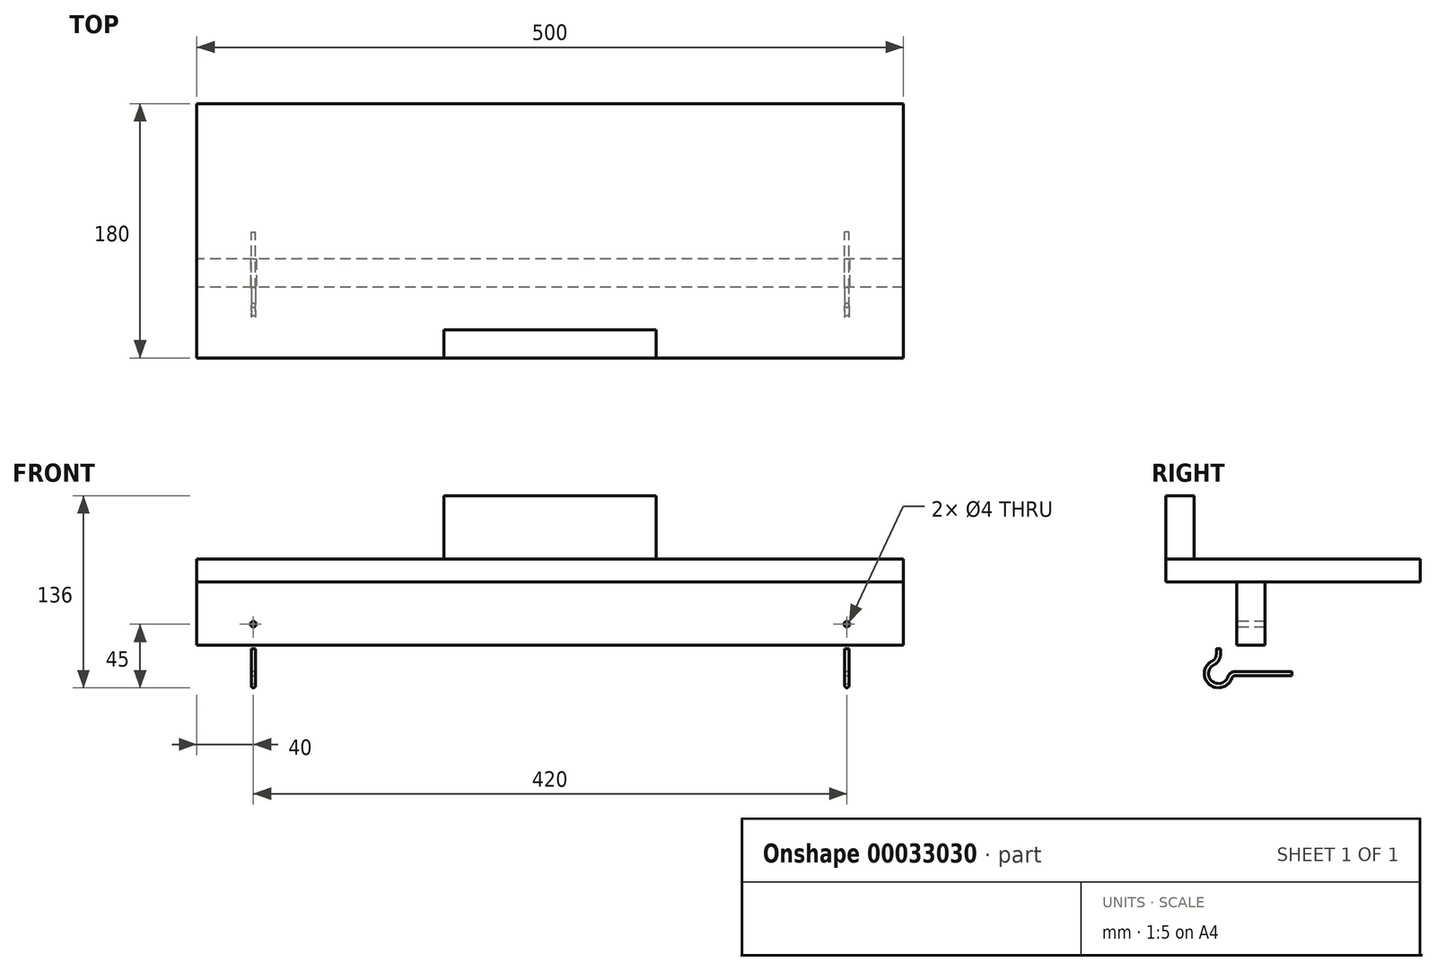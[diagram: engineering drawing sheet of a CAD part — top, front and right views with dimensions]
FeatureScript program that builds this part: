
annotation { "Feature Type Name" : "Feature", "Feature Type Description" : "" }
export const myFeature = defineFeature(function(context is Context, id is Id, definition is map)
    precondition{}
    {
        {
            var Q0;
            Q0=qCreatedBy(makeId("Right.planeOp"),FACE);
            var sketch = newSketch(context, id + "F0", { "sketchPlane" : qUnion([Q0])});
            skLineSegment(sketch, "E0.bottom", {"start": v(0, 0) * mm, "end": v(-180, 0) * mm});
            skLineSegment(sketch, "E0.top", {"start": v(0, -16) * mm, "end": v(-180, -16) * mm});
            skLineSegment(sketch, "E0.left", {"start": v(0, 0) * mm, "end": v(0, -16) * mm});
            skLineSegment(sketch, "E0.right", {"start": v(-180, 0) * mm, "end": v(-180, -16) * mm});
            skSolve(sketch);
        }
        {
            var Q0;
            Q0 = qSketchRegion(id + "F0", true);
            extrude(context, id + "F1", {"entities" : qUnion([Q0]), "endBound" : BoundingType.SYMMETRIC, "depth" : 500 * mm});
        }
        {
            var Q0;
            Q0=qCreatedBy(makeId("Right.planeOp"),FACE);
            var sketch = newSketch(context, id + "F2", { "sketchPlane" : qUnion([Q0])});
            skLineSegment(sketch, "E1.bottom", {"start": v(-130, -16) * mm, "end": v(-110, -16) * mm});
            skLineSegment(sketch, "E1.top", {"start": v(-130, -61) * mm, "end": v(-110, -61) * mm});
            skLineSegment(sketch, "E1.left", {"start": v(-130, -16) * mm, "end": v(-130, -61) * mm});
            skLineSegment(sketch, "E1.right", {"start": v(-110, -16) * mm, "end": v(-110, -61) * mm});
            skSolve(sketch);
        }
        {
            var Q0;
            Q0 = qSketchRegion(id + "F2", true);
            var Q1;
            Q1=makeQuery(id+"F1.opExtrude","CAP_FACE",FACE,{"disambiguationData":[OSD([sQuery(id+"F0.wireOp",EDGE,"E0.bottom"),sQuery(id+"F0.wireOp",EDGE,"E0.top"),sQuery(id+"F0.wireOp",EDGE,"E0.left"),sQuery(id+"F0.wireOp",EDGE,"E0.right")])],"isStart":false});
            var Q2;
            Q2=makeQuery(id+"F1.opExtrude","CAP_FACE",FACE,{"disambiguationData":[OSD([sQuery(id+"F0.wireOp",EDGE,"E0.bottom"),sQuery(id+"F0.wireOp",EDGE,"E0.top"),sQuery(id+"F0.wireOp",EDGE,"E0.left"),sQuery(id+"F0.wireOp",EDGE,"E0.right")])],"isStart":true});
            extrude(context, id + "F3", {"entities" : qUnion([Q0]), "endBound" : BoundingType.UP_TO_SURFACE, "endBoundEntityFace" : qUnion([Q1]), "depth" : 25 * mm, "hasSecondDirection" : true, "secondDirectionBound" : SecondDirectionBoundingType.UP_TO_SURFACE, "secondDirectionOppositeDirection" : true, "secondDirectionBoundEntityFace" : qUnion([Q2]), "secondDirectionDepth" : 25 * mm});
        }
        {
            var Q0;
            Q0=makeQuery(id+"F3.opExtrude","CAP_FACE",FACE,{"disambiguationData":[OSD([sQuery(id+"F2.wireOp",EDGE,"E1.bottom"),sQuery(id+"F2.wireOp",EDGE,"E1.top"),sQuery(id+"F2.wireOp",EDGE,"E1.left"),sQuery(id+"F2.wireOp",EDGE,"E1.right")])],"isStart":false});
            cPlane(context, id + "F4", {"entities" : qUnion([Q0]), "cplaneType" : CPlaneType.OFFSET, "offset" : 40 * mm, "oppositeDirection" : true, "width" : 150 * mm, "height" : 150 * mm});
        }
        {
            var Q0;
            Q0=makeQuery(id+"F3.opExtrude","SWEPT_FACE",FACE,{"disambiguationData":[OSD([sQuery(id+"F2.wireOp",EDGE,"E1.left")])]});
            var sketch = newSketch(context, id + "F5", { "sketchPlane" : qUnion([Q0])});
            skCircle(sketch, "E2", {"center": v(210, -46) * mm, "radius": 2 * mm});
            skCircle(sketch, "E3", {"center": v(-210, -46) * mm, "radius": 2 * mm});
            skLineSegment(sketch, "E4", {"start": v(-210, -46) * mm, "end": v(210, -46) * mm, "construction": true});
            skPoint(sketch, "E5", {"position": v(0, -46) * mm});
            skSolve(sketch);
        }
        {
            var Q0;
            Q0 = qSketchRegion(id + "F5", true);
            extrude(context, id + "F6", {"entities" : qUnion([Q0]), "operationType" : NewBodyOperationType.REMOVE, "endBound" : BoundingType.UP_TO_NEXT, "oppositeDirection" : true, "depth" : 25 * mm});
        }
        {
            var Q0;
            Q0=qCreatedBy(id+"F4.planeOp",FACE);
            var sketch = newSketch(context, id + "F7", { "sketchPlane" : qUnion([Q0])});
            skLineSegment(sketch, "E6", {"start": v(-91, -81) * mm, "end": v(-131, -81) * mm});
            skArc(sketch, "E7", {"start": v(-131, -81) * mm, "mid": v(-133.33, -81.75) * mm, "end": v(-134.79, -83.72) * mm});
            skArc(sketch, "E8", {"start": v(-146.68, -73.42) * mm, "mid": v(-148.4, -87.42) * mm, "end": v(-134.79, -83.72) * mm});
            skLineSegment(sketch, "E9", {"start": v(-142.84, -67.17) * mm, "end": v(-142.84, -63.5) * mm});
            skPoint(sketch, "E10.visualSharp", {"position": v(-142.84, -72.5) * mm});
            skArc(sketch, "E10.filletArc", {"start": v(-146.68, -73.42) * mm, "mid": v(-143.88, -70.84) * mm, "end": v(-142.84, -67.17) * mm});
            skSolve(sketch);
        }
        {
            var Q0;
            Q0=sQuery(id+"F7.wireOp",VERTEX,"E9.end");
            var Q1;
            Q1=sQuery(id+"F7.wireOp",EDGE,"E9");
            cPlane(context, id + "F8", {"entities" : qUnion([Q0, Q1]), "cplaneType" : CPlaneType.CURVE_POINT, "offset" : 150 * mm, "width" : 150 * mm, "height" : 150 * mm});
        }
        {
            var Q0;
            Q0=qCreatedBy(id+"F8.planeOp",FACE);
            var sketch = newSketch(context, id + "F9", { "sketchPlane" : qUnion([Q0])});
            skCircle(sketch, "E11", {"center": v(210, -142.84) * mm, "radius": 1.5 * mm});
            skSolve(sketch);
        }
        {
            var Q0;
            Q0 = qSketchRegion(id + "F9", true);
            var Q1;
            Q1 = qConstructionFilter(qBodyType(qCreatedBy(id + "F7" ,EDGE), BodyType.WIRE), ConstructionObject.NO);
            sweep(context, id + "F10", {"profiles" : qUnion([Q0]), "path" : qUnion([Q1])});
        }
        {
            var Q0;
            Q0=makeQuery(id+"F10.opSweep","SWEPT_BODY",BODY,{"disambiguationData":[OSD([sQuery(id+"F7.wireOp",EDGE,"E8"),sQuery(id+"F9.wireOp",EDGE,"E11")])]});
            var Q1;
            Q1=qCreatedBy(makeId("Right.planeOp"),FACE);
            mirror(context, id + "F11", {"operationType" : NewBodyOperationType.ADD, "entities" : qUnion([Q0]), "mirrorPlane" : qUnion([Q1])});
        }
        {
            var Q0;
            Q0=qCreatedBy(makeId("Right.planeOp"),FACE);
            var sketch = newSketch(context, id + "F12", { "sketchPlane" : qUnion([Q0])});
            skLineSegment(sketch, "E12.bottom", {"start": v(-160, 45) * mm, "end": v(-180, 45) * mm});
            skLineSegment(sketch, "E12.top", {"start": v(-160, 0) * mm, "end": v(-180, 0) * mm});
            skLineSegment(sketch, "E12.left", {"start": v(-160, 45) * mm, "end": v(-160, 0) * mm});
            skLineSegment(sketch, "E12.right", {"start": v(-180, 45) * mm, "end": v(-180, 0) * mm});
            skSolve(sketch);
        }
        {
            var Q0;
            Q0=makeQuery(id+"F12.imprint","IMPRINT",FACE,{"disambiguationData":[TD([[makeQuery(id+"F12.imprint","IMPRINT",EDGE,{"derivedFrom":sQuery(id+"F12.wireOp",EDGE,"E12.bottom")}),1.0]])]});
            extrude(context, id + "F13", {"entities" : qUnion([Q0]), "endBound" : BoundingType.SYMMETRIC, "depth" : 150 * mm});
        }
    });
